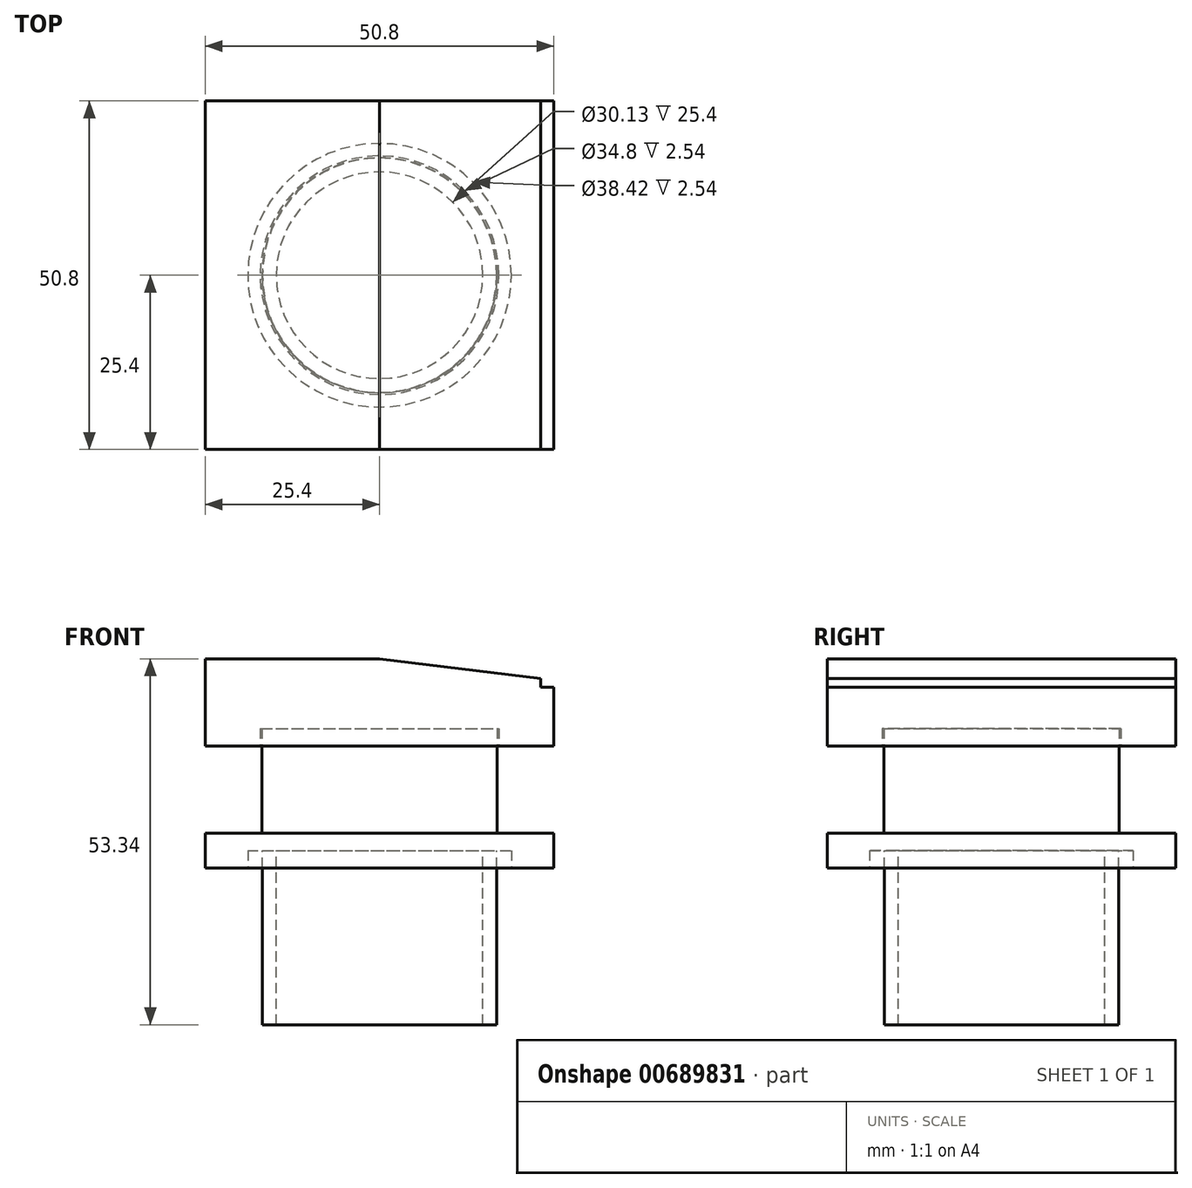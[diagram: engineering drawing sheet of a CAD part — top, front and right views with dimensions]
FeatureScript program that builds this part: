
annotation { "Feature Type Name" : "Feature", "Feature Type Description" : "" }
export const myFeature = defineFeature(function(context is Context, id is Id, definition is map)
    precondition{}
    {
        {
            var Q0;
            Q0=qCreatedBy(makeId("Front.planeOp"),FACE);
            var sketch = newSketch(context, id + "F0", { "sketchPlane" : qUnion([Q0])});
            skLineSegment(sketch, "E0.bottom", {"start": v(-25.4, 0) * mm, "end": v(25.4, 0) * mm});
            skLineSegment(sketch, "E0.top", {"start": v(-25.4, -12.7) * mm, "end": v(25.4, -12.7) * mm});
            skLineSegment(sketch, "E0.left", {"start": v(-25.4, 0) * mm, "end": v(-25.4, -12.7) * mm});
            skLineSegment(sketch, "E0.right", {"start": v(25.4, 0) * mm, "end": v(25.4, -12.7) * mm});
            skSolve(sketch);
        }
        {
            var Q0;
            Q0 = qSketchRegion(id + "F0", true);
            extrude(context, id + "F1", {"entities" : qUnion([Q0]), "endBound" : BoundingType.SYMMETRIC, "depth" : 50.8 * mm, "offsetDistance" : 25.4 * mm});
        }
        {
            var Q0;
            Q0=qCreatedBy(makeId("Front.planeOp"),FACE);
            var sketch = newSketch(context, id + "F2", { "sketchPlane" : qUnion([Q0])});
            skLineSegment(sketch, "E1", {"start": v(0, 0) * mm, "end": v(23.5, -2.86) * mm});
            skLineSegment(sketch, "E2", {"start": v(23.5, -2.86) * mm, "end": v(23.5, -4.15) * mm});
            skLineSegment(sketch, "E3", {"start": v(23.5, -4.15) * mm, "end": v(25.4, -4.15) * mm});
            skLineSegment(sketch, "E4", {"start": v(25.4, -4.15) * mm, "end": v(25.4, -12.7) * mm});
            skLineSegment(sketch, "E5", {"start": v(25.4, -12.7) * mm, "end": v(40.84, -12.7) * mm});
            skLineSegment(sketch, "E6", {"start": v(40.84, -12.7) * mm, "end": v(40.84, 0) * mm});
            skLineSegment(sketch, "E7", {"start": v(40.84, 0) * mm, "end": v(0, 0) * mm});
            skSolve(sketch);
        }
        {
            var Q0;
            Q0 = qSketchRegion(id + "F2", true);
            extrude(context, id + "F3", {"entities" : qUnion([Q0]), "operationType" : NewBodyOperationType.REMOVE, "endBound" : BoundingType.SYMMETRIC, "oppositeDirection" : true, "depth" : 50.8 * mm, "offsetDistance" : 25.4 * mm});
        }
        {
            var Q0;
            Q0=qCreatedBy(makeId("Front.planeOp"),FACE);
            var sketch = newSketch(context, id + "F4", { "sketchPlane" : qUnion([Q0])});
            skLineSegment(sketch, "E8", {"start": v(0, -1.4) * mm, "end": v(0, -17.06) * mm});
            skSolve(sketch);
        }
        {
            var Q0;
            Q0=makeQuery(id+"F1.opExtrude","SWEPT_FACE",FACE,{"disambiguationData":[OSD([sQuery(id+"F0.wireOp",EDGE,"E0.top")])]});
            var sketch = newSketch(context, id + "F5", { "sketchPlane" : qUnion([Q0])});
            skCircle(sketch, "E9", {"center": v(0, 0) * mm, "radius": 17.4 * mm});
            skSolve(sketch);
        }
        {
            var Q0;
            Q0 = qSketchRegion(id + "F5", true);
            extrude(context, id + "F6", {"entities" : qUnion([Q0]), "operationType" : NewBodyOperationType.REMOVE, "oppositeDirection" : true, "depth" : 2.54 * mm, "offsetDistance" : 25.4 * mm});
        }
        {
            var Q0;
            Q0=qCreatedBy(makeId("Front.planeOp"),FACE);
            var sketch = newSketch(context, id + "F7", { "sketchPlane" : qUnion([Q0])});
            skLineSegment(sketch, "E10.bottom", {"start": v(-25.4, -25.4) * mm, "end": v(25.4, -25.4) * mm});
            skLineSegment(sketch, "E10.top", {"start": v(-25.4, -30.48) * mm, "end": v(25.4, -30.48) * mm});
            skLineSegment(sketch, "E10.left", {"start": v(-25.4, -25.4) * mm, "end": v(-25.4, -30.48) * mm});
            skLineSegment(sketch, "E10.right", {"start": v(25.4, -25.4) * mm, "end": v(25.4, -30.48) * mm});
            skSolve(sketch);
        }
        {
            var Q0;
            Q0 = qSketchRegion(id + "F7", true);
            extrude(context, id + "F8", {"entities" : qUnion([Q0]), "endBound" : BoundingType.SYMMETRIC, "depth" : 50.8 * mm, "offsetDistance" : 25.4 * mm});
        }
        {
            var Q0;
            Q0=makeQuery(id+"F8.opExtrude","SWEPT_FACE",FACE,{"disambiguationData":[OSD([sQuery(id+"F7.wireOp",EDGE,"E10.bottom")])]});
            var sketch = newSketch(context, id + "F9", { "sketchPlane" : qUnion([Q0])});
            skCircle(sketch, "E11", {"center": v(0, 0) * mm, "radius": 17.15 * mm});
            skSolve(sketch);
        }
        {
            var Q0;
            Q0 = qSketchRegion(id + "F9", true);
            var Q1;
            Q1=makeQuery(id+"F6.boolean.opBoolean","COPY",FACE,{"derivedFrom":makeQuery(id+"F6.opExtrude","CAP_FACE",FACE,{"disambiguationData":[OSD([sQuery(id+"F5.wireOp",EDGE,"E9")])],"isStart":false})});
            extrude(context, id + "F10", {"entities" : qUnion([Q0]), "operationType" : NewBodyOperationType.ADD, "endBound" : BoundingType.UP_TO_SURFACE, "depth" : 25.4 * mm, "endBoundEntityFace" : qUnion([Q1]), "offsetDistance" : 25.4 * mm});
        }
        {
            var Q0;
            Q0=makeQuery(id+"F8.opExtrude","SWEPT_FACE",FACE,{"disambiguationData":[OSD([sQuery(id+"F7.wireOp",EDGE,"E10.top")])]});
            var sketch = newSketch(context, id + "F11", { "sketchPlane" : qUnion([Q0])});
            skCircle(sketch, "E12", {"center": v(0, 0) * mm, "radius": 19.21 * mm});
            skSolve(sketch);
        }
        {
            var Q0;
            Q0 = qSketchRegion(id + "F11", true);
            extrude(context, id + "F12", {"entities" : qUnion([Q0]), "operationType" : NewBodyOperationType.REMOVE, "oppositeDirection" : true, "depth" : 2.54 * mm, "offsetDistance" : 25.4 * mm});
        }
        {
            var Q0;
            Q0=makeQuery(id+"F12.boolean.opBoolean","COPY",FACE,{"derivedFrom":makeQuery(id+"F12.opExtrude","CAP_FACE",FACE,{"disambiguationData":[OSD([sQuery(id+"F11.wireOp",EDGE,"E12")])],"isStart":false})});
            var sketch = newSketch(context, id + "F13", { "sketchPlane" : qUnion([Q0])});
            skCircle(sketch, "E13", {"center": v(0, 0) * mm, "radius": 17.07 * mm});
            skCircle(sketch, "E14", {"center": v(0, 0) * mm, "radius": 15.06 * mm});
            skSolve(sketch);
        }
        {
            var Q0;
            Q0 = qSketchRegion(id + "F13", true);
            extrude(context, id + "F14", {"entities" : qUnion([Q0]), "depth" : 25.4 * mm, "offsetDistance" : 25.4 * mm});
        }
    });
